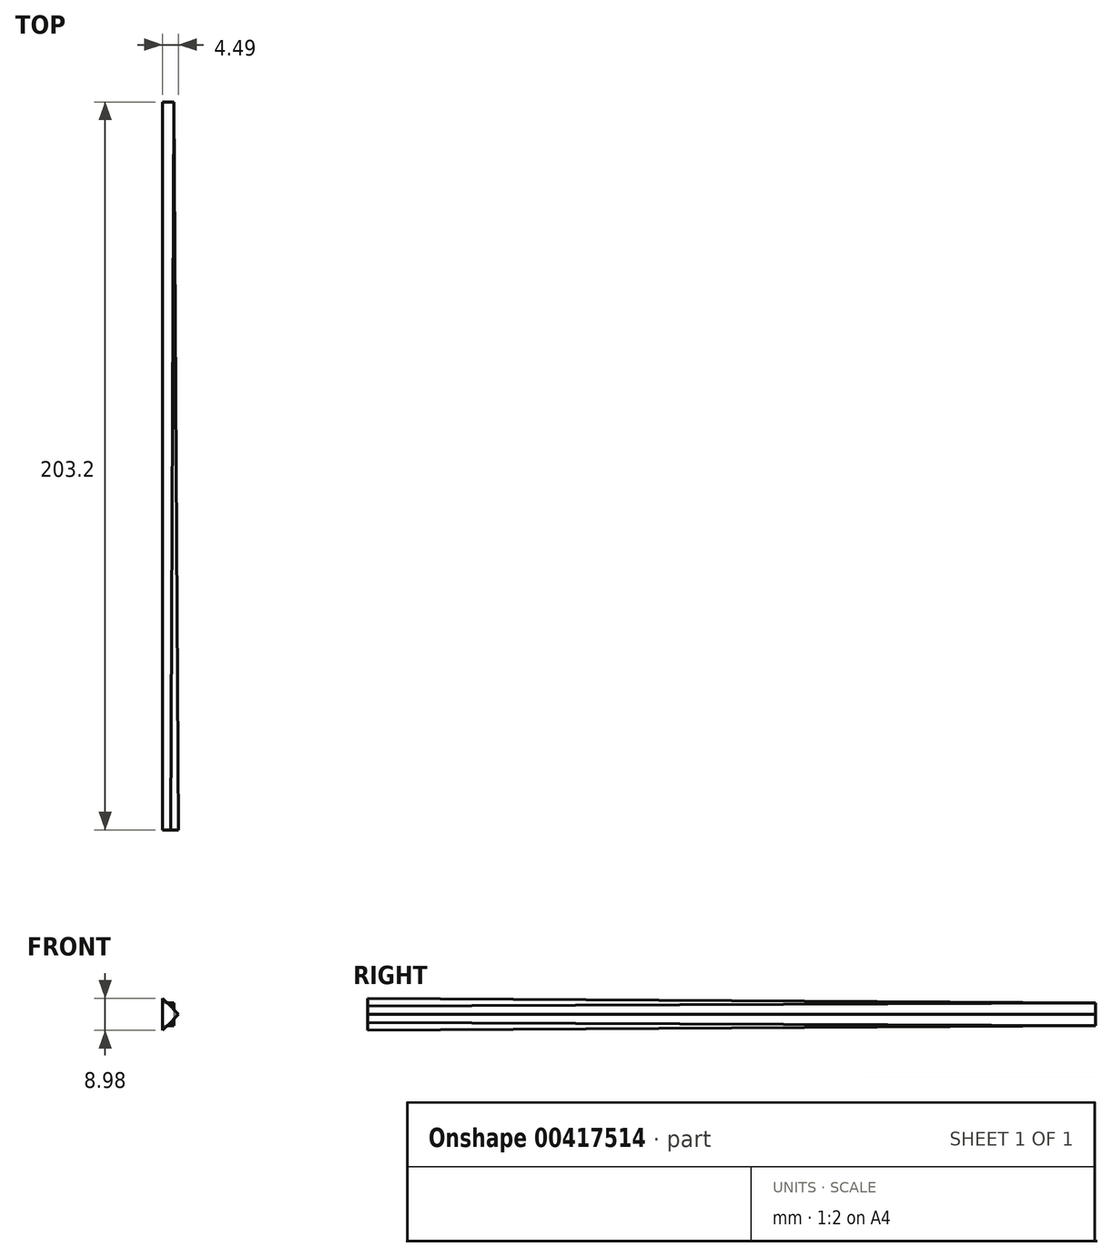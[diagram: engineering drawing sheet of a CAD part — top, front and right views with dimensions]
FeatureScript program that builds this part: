
annotation { "Feature Type Name" : "Feature", "Feature Type Description" : "" }
export const myFeature = defineFeature(function(context is Context, id is Id, definition is map)
    precondition{}
    {
        {
            var Q0;
            Q0=qCreatedBy(makeId("Front.planeOp"),FACE);
            var sketch = newSketch(context, id + "F0", { "sketchPlane" : qUnion([Q0])});
            skLineSegment(sketch, "E0.bottom", {"start": v(-3.17, 3.17) * mm, "end": v(3.18, 3.17) * mm});
            skLineSegment(sketch, "E0.top", {"start": v(-3.18, -3.17) * mm, "end": v(3.17, -3.17) * mm});
            skLineSegment(sketch, "E0.left", {"start": v(-3.17, 3.17) * mm, "end": v(-3.18, -3.17) * mm});
            skLineSegment(sketch, "E0.right", {"start": v(3.18, 3.17) * mm, "end": v(3.17, -3.17) * mm});
            skPoint(sketch, "E0.middle", {"position": v(0, 0) * mm});
            skLineSegment(sketch, "E1", {"start": v(-3.17, 0) * mm, "end": v(3.17, 0) * mm, "construction": true});
            skLineSegment(sketch, "E2", {"start": v(0, 3.17) * mm, "end": v(0, -3.17) * mm, "construction": true});
            skSolve(sketch);
        }
        {
            var Q0;
            Q0=qCreatedBy(makeId("Front.planeOp"),FACE);
            cPlane(context, id + "F1", {"entities" : qUnion([Q0]), "cplaneType" : CPlaneType.OFFSET, "offset" : 203.2 * mm, "width" : 152.4 * mm, "height" : 152.4 * mm});
        }
        {
            var Q0;
            Q0=qCreatedBy(id+"F1.planeOp",FACE);
            var sketch = newSketch(context, id + "F2", { "sketchPlane" : qUnion([Q0])});
            skLineSegment(sketch, "E3.bottom", {"start": v(4.5, 0) * mm, "end": v(0, 4.5) * mm});
            skLineSegment(sketch, "E3.top", {"start": v(0, -4.5) * mm, "end": v(-4.5, 0) * mm});
            skLineSegment(sketch, "E3.left", {"start": v(4.5, 0) * mm, "end": v(0, -4.5) * mm});
            skLineSegment(sketch, "E3.right", {"start": v(0, 4.5) * mm, "end": v(-4.5, 0) * mm});
            skPoint(sketch, "E3.middle", {"position": v(0, 0) * mm});
            skLineSegment(sketch, "E4", {"start": v(0, 4.5) * mm, "end": v(0, -4.5) * mm, "construction": true});
            skLineSegment(sketch, "E5", {"start": v(-4.5, 0) * mm, "end": v(4.5, 0) * mm, "construction": true});
            skSolve(sketch);
        }
        {
            var Q0;
            Q0=qCreatedBy(makeId("Right.planeOp"),FACE);
            var sketch = newSketch(context, id + "F3", { "sketchPlane" : qUnion([Q0])});
            skLineSegment(sketch, "E6", {"start": v(-203.2, 4.5) * mm, "end": v(0, 3.18) * mm});
            skLineSegment(sketch, "E7", {"start": v(-203.2, 0) * mm, "end": v(0, 0) * mm, "construction": true});
            skLineSegment(sketch, "E8.MirrorCS", {"start": v(-203.2, -4.5) * mm, "end": v(0, -3.17) * mm});
            skSolve(sketch);
        }
        {
            var Q0;
            Q0 = qSketchRegion(id + "F0", true);
            var Q1;
            Q1 = qSketchRegion(id + "F2", true);
            var Q2;
            Q2=sQuery(id+"F3.wireOp",EDGE,"E6");
            var Q3;
            Q3=sQuery(id+"F3.wireOp",EDGE,"E8.MirrorCS");
            var Q4;
            Q4=sQuery(id+"F2.wireOp",VERTEX,"E5.end");
            var Q5;
            Q5=sQuery(id+"F0.wireOp",VERTEX,"E1.end");
            loft(context, id + "F4", {"addGuides" : true, "sheetProfilesArray" : [{ "sheetProfileEntities" : qUnion([Q0]) }, { "sheetProfileEntities" : qUnion([Q1]) }], "guidesArray" : [{ "guideEntities" : qUnion([Q2]), "guideDerivativeType" : LoftGuideDerivativeType.DEFAULT, "guideDerivativeMagnitude" : 1 }, { "guideEntities" : qUnion([Q3]), "guideDerivativeType" : LoftGuideDerivativeType.DEFAULT, "guideDerivativeMagnitude" : 1 }], "matchConnections" : true, "connections" : [{ "connectionEntities" : qUnion([Q4, Q5]), "connectionEdgeQueries" : qUnion([]), "connectionEdgeParameters" : [] }]});
        }
        {
            var Q0;
            Q0=qCreatedBy(makeId("Top.planeOp"),FACE);
            var sketch = newSketch(context, id + "F5", { "sketchPlane" : qUnion([Q0])});
            skLineSegment(sketch, "E9.bottom", {"start": v(-20.68, 88.15) * mm, "end": v(0, 88.15) * mm});
            skLineSegment(sketch, "E9.top", {"start": v(-20.68, -237.48) * mm, "end": v(0, -237.48) * mm});
            skLineSegment(sketch, "E9.left", {"start": v(-20.68, 88.15) * mm, "end": v(-20.68, -237.48) * mm});
            skLineSegment(sketch, "E9.right", {"start": v(0, 88.15) * mm, "end": v(0, -237.48) * mm});
            skSolve(sketch);
        }
        {
            var Q0;
            Q0 = qSketchRegion(id + "F5", true);
            extrude(context, id + "F6", {"entities" : qUnion([Q0]), "operationType" : NewBodyOperationType.REMOVE, "endBound" : BoundingType.SYMMETRIC, "depth" : 25.4 * mm});
        }
    });
